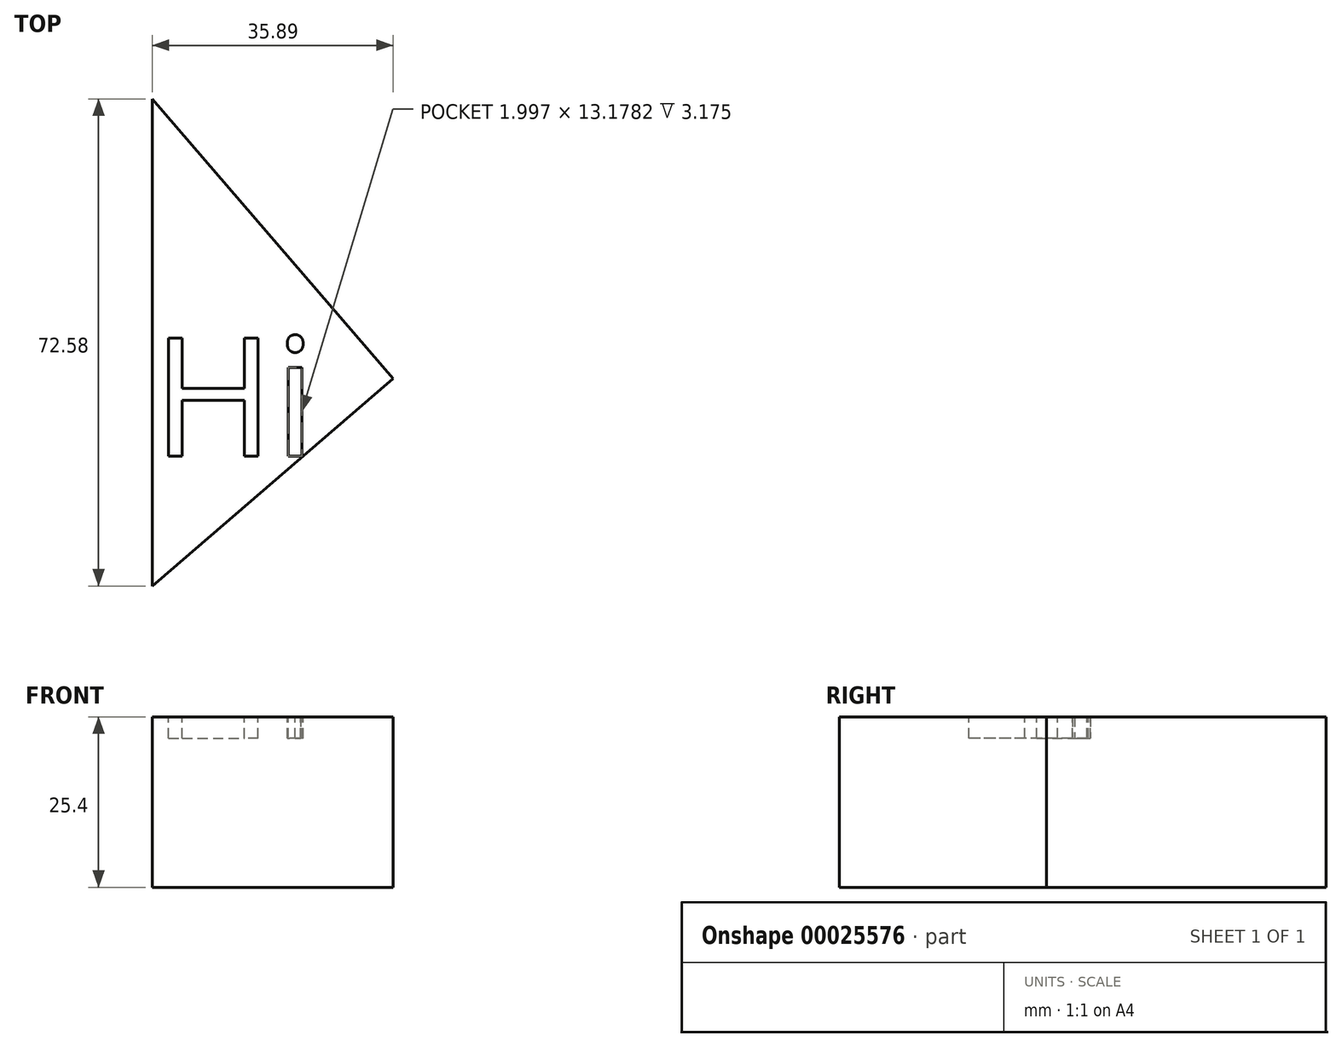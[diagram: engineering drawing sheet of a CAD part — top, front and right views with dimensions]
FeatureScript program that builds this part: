
annotation { "Feature Type Name" : "Feature", "Feature Type Description" : "" }
export const myFeature = defineFeature(function(context is Context, id is Id, definition is map)
    precondition{}
    {
        {
            var Q0;
            Q0=qCreatedBy(makeId("Top.planeOp"),FACE);
            var sketch = newSketch(context, id + "F0", { "sketchPlane" : qUnion([Q0])});
            skLineSegment(sketch, "E0", {"start": v(0, 0) * mm, "end": v(35.89, 30.91) * mm});
            skLineSegment(sketch, "E1", {"start": v(35.89, 30.91) * mm, "end": v(0, 72.58) * mm});
            skLineSegment(sketch, "E2", {"start": v(0, 72.58) * mm, "end": v(0, 0) * mm});
            skSolve(sketch);
        }
        {
            var Q0;
            Q0=makeQuery(id+"F0.imprint","IMPRINT",FACE,{"disambiguationData":[TD([[makeQuery(id+"F0.imprint","IMPRINT",EDGE,{"derivedFrom":sQuery(id+"F0.wireOp",EDGE,"E0")}),1.0]])]});
            extrude(context, id + "F1", {"entities" : qUnion([Q0]), "depth" : 25.4 * mm});
        }
        {
            var Q0;
            Q0=makeQuery(id+"F1.opExtrude","CAP_FACE",FACE,{"disambiguationData":[OSD([sQuery(id+"F0.wireOp",EDGE,"E0"),sQuery(id+"F0.wireOp",EDGE,"E1"),sQuery(id+"F0.wireOp",EDGE,"E2")])],"isStart":false});
            var sketch = newSketch(context, id + "F2", { "sketchPlane" : qUnion([Q0])});
            skText(sketch, "E3", { "text": "Hi", "fontName": "OpenSans-Regular.ttf"});
            const initialGuessF2  = {"E3": [0, 0.01936, 1, 0, 0.01773]};
            skSetInitialGuess(sketch, initialGuessF2);
            skSolve(sketch);
        }
        {
            var Q0;
            Q0 = qSketchRegion(id + "F2", true);
            extrude(context, id + "F3", {"entities" : qUnion([Q0]), "operationType" : NewBodyOperationType.REMOVE, "oppositeDirection" : true, "depth" : 3.17 * mm});
        }
    });
